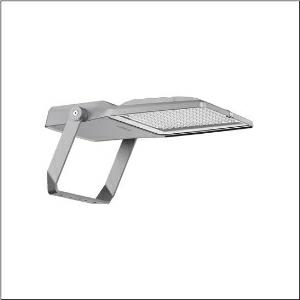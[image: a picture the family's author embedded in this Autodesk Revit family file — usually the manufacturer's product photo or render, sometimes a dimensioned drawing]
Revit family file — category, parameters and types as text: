
# Revit family: floodlight_fl_21_iq_midi___rs12_5xa7781f6b1a_422c
name_source: partatom
category: Lighting Fixtures
units: mm (PartAtom-declared; Revit-internal decimal feet)

## family parameters
Cut with Voids When Loaded = No
Host = Face
Light Source = No
Part Type = Normal
Room Calculation Point = No
Round Connector Dimension = Use Diameter
Shared = No

## types (1)
- --- (1 x LED, 28520 lm, 270.2 W, 5700K)
    Apparent Load = 270 VA
    CIE Flux Codes = 79 92 99 100 100
    Color Rendering = 90
    Color Temperature = 5700K
    Default Elevation = 1800 mm
    Description = Floodlight FL 21 iQ midi, floodlight, primary light control with lens, of PMMA, primary optical cover: protective disc, of toughened safety glass, transparent, light distribution: RS12, light emission: direct distribution, installation type: surface-mounted, LED, High Power LED, rated luminous flux: 28.520lm, luminous efficacy: 106lm/W, light colour: 957, colour temperature: 5700K, control gear: iQ Comfort/DALI, control: optimised constant luminous flux control (CLO 2.0), Desk-Remote (wireless, voltage-free reading and setting of iQ features in the workshop via application-optimized NFC function/RFID function), Light-Fading, Smart-Wire, Night-Set, Lumen-Switch, Temp-Guard, Auto-Match, with terminal, 6-pole, mains connection: 220..240V, AC, 50/60Hz, start of lifetime: 270W, end of service life: 287W, reduction: 117W, luminaire housing, of diecast aluminium, powder-coated, Siteco® metallic grey (DB 702S), corrosivity category C5 mid according to DIN EN ISO 12944, suitable for swimming pools, chlorine-resistant, sealing non-destructively replaceable, mounting bracket, of steel, galvanised, powder-coated, Siteco® metallic grey (DB 702S), protection rating (complete): IP66, insulation class (complete): insulation class II (safety insulation), certification: CE, ENEC, VDE, protection symbol: D, impact resistance: IK08, permissible operating ambient temperature: -40..+40°C, permissible operating ambient temperature for outdoor applications: -40..+50°C, standard: DIN EN 12944, LABS conformity tested according to VDMA 24364:2018-05, packaging unit: 1 piece

Light Distribution: RS12
    Height = 76 mm
    Lamp = 1 x LED
    Lamp Light Flux = 28520 lm
    Lamp Power = 270.2 W
    Lamp count = 1
    Length = 657 mm
    Luminous efficacy = 106 lm/W
    Manufacturer = Siteco
    ModVariant = No
    Model = 5XA7781F6B1A
    Number of Poles = 1
    OnlyDefault = Yes
    Power Factor = 1
    Product Name = Floodlight FL 21 iQ midi | RS12
    Product group = floodlight | pylon annexe
    ProductGroupID = 6200
    Protection Class = Protection class II
    Protection Degree = IP 66
    RLX_Detail_Level = 1
    RLX_Emergency_Light_Flux = 0 lm
    RLX_Emergency_Type = 0
    RLX_Emergency_Type_DB = No
    RlxData = <blob elided: 141097 chars, md5=ad8394ee>
    Socket = socket
    Standby Power = 0 W
    System Light Flux = 28520 lm
    System Power = 270 W
    Type Comments = factory setting: luminous flux: 100 % | dim-lin: 254 | 620 mA
    Type Image = l_1006876.jpg
    URL = http://relux.com
    VarID = @adj_107362
    Voltage = 0 V
    Weight = 0.00 kg
    Width = 442 mm

## geometry (parser evidence)
native form markers: Blend x5, Sweep x13
no freeform markers — native parametric forms only
